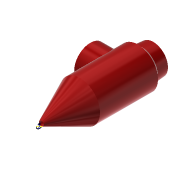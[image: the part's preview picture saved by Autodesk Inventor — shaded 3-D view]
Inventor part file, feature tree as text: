
AUTODESK INVENTOR PART (.ipt)
format: ipt  version: 2019.4 (Build 234330000, 330)  size: 177,664 bytes
history: native  units: mm
features: sketch x5, extrude x3, other x3, reference x2, revolve x1, plane x1, projected_geometry x1
ambient origin geometry x8: Origin, YZ Plane, XZ Plane, XY Plane, X Axis, Y Axis, Z Axis, Center Point
bodies: Solid1 (feature_tree)
feature tree (16):
  revolve  "Revolution1"  [1 undecoded]
  sketch  "Sketch2"  dims[d6=90.0deg d7=2.0mm]
  sketch  "Sketch3"  dims[d8=19.0mm d9=15.0mm d10=0.0mm]
  plane  "Work Plane1"
  extrude  "Extrusion1"  Depth=2.0mm
  extrude  "Extrusion2"  Depth=15.0mm TaperAngle=0.0deg
  extrude  "Extrusion3"  Depth=15.0mm TaperAngle=0.0deg
  sketch  "Sketch1"  dims[d4=4.0mm d5=4.0mm]
  reference  "Reference1"
  reference  "Reference2"
  sketch  "Sketch4"  dims[d11=15.5mm d12=15.0mm d13=0.0mm]
  projected_geometry  "Projected Loop1"
  sketch  "Sketch5"  dims[d14=15.0mm d15=-0.872665mm]
  other  "Assemlby_OpenOxygen.iam"
  other  "00_Sensirion_Flowsensor:1"
  other  "00_Oxygen_Oxi:1"
note: 1 required parameter value undecoded (feature->parameter linkage not recoverable at this tier; creation-order binding heuristic only, values carry confidence <= 0.55)
